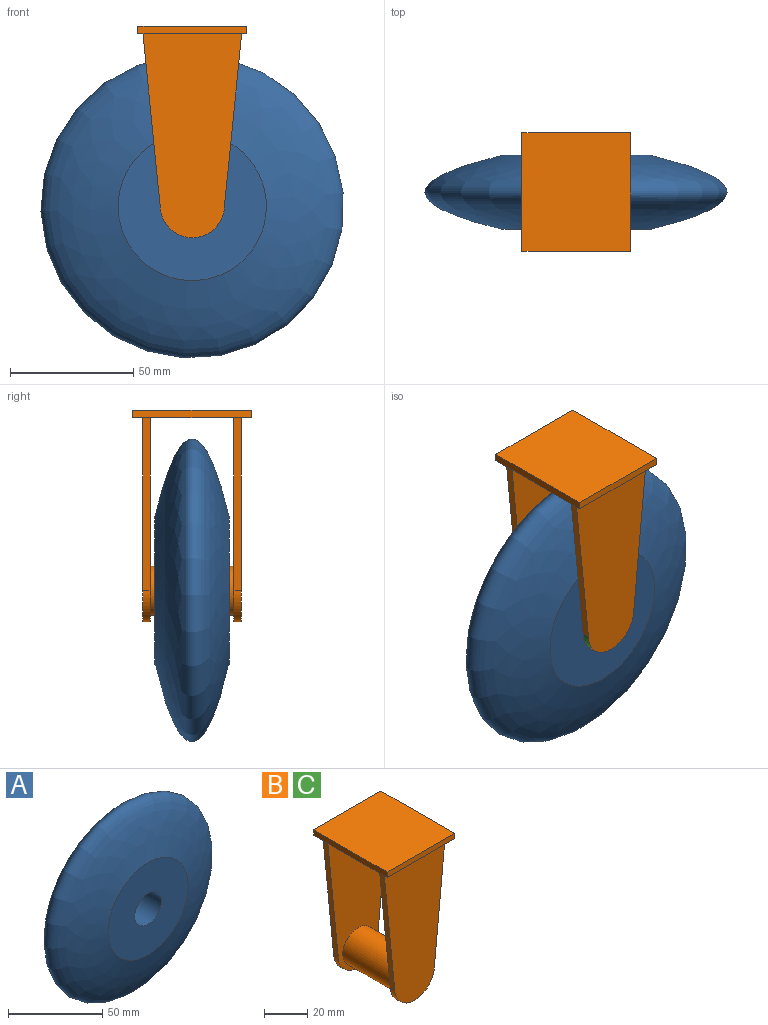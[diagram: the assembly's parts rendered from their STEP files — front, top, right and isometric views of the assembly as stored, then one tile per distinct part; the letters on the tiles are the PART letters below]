
ASSEMBLY  parts=3 mates=1
PART A: 4 faces, bbox 122.7x30x122.7 mm
  f0: plane 60x60mm, normal (0,1,0), area 2513.3mm2, adj f1,f3
  f1: cylinder r=10mm len=30mm, axis (0,1,0), area 1885mm2, adj f0,f2
  f2: plane 60x60mm, normal (0,-1,0), area 2513.3mm2, adj f1,f3
  f3: revolved ~122.66x122.66mm, area 21283.1mm2, adj f0,f2
PART B: 17 faces, bbox 44x48x85.7 mm
  f0: cylinder r=10mm len=34mm, axis (0,1,0), area 2136.3mm2, adj f4,f9
  f1: plane 70x7.01mm, normal (-1,0,-0.1), area 211.1mm2, adj f2,f4,f5,f11
  f2: cylinder r=13mm len=25.99mm, axis (0,-1,0), area 120.5mm2, adj f1,f3,f4,f5
  f3: plane 70x7mm, normal (1,0,-0.1), area 211mm2, adj f2,f4,f5,f11
  f4: plane 82.66x40mm, normal (0,1,0), area 2252.1mm2, adj f0,f1,f2,f3,f11
  f5: plane 82.66x40mm, normal (0,-1,0), area 2566.2mm2, adj f1,f2,f3,f11
  f6: plane 70x7.01mm, normal (-1,0,-0.1), area 211.1mm2, adj f7,f9,f10,f11
  f7: cylinder r=13mm len=25.99mm, axis (0,1,0), area 120.5mm2, adj f6,f8,f9,f10
  f8: plane 70x7mm, normal (1,0,-0.1), area 211mm2, adj f7,f9,f10,f11
  f9: plane 82.66x40mm, normal (0,-1,0), area 2252.1mm2, adj f0,f6,f7,f8,f11
  f10: plane 82.66x40mm, normal (0,1,0), area 2566.2mm2, adj f6,f7,f8,f11
  f11: plane 48x44mm, normal (0,0,-1), area 1872mm2, adj f1,f3,f4,f5,f6,f8,f9,f10
  f12: plane 44x3mm, normal (0,1,0), area 132mm2, adj f11,f13,f15,f16
  f13: plane 48x3mm, normal (-1,0,0), area 144mm2, adj f11,f12,f14,f16
  f14: plane 44x3mm, normal (0,-1,0), area 132mm2, adj f11,f13,f15,f16
  f15: plane 48x3mm, normal (1,0,0), area 144mm2, adj f11,f12,f14,f16
  f16: plane 48x44mm, normal (0,0,1), area 2112mm2, adj f12,f13,f14,f15
PART C: same geometry as B
PLACE A t=(-39.25,44.98,71.29)mm
PLACE B t=(-39.25,44.98,71.29)mm
PLACE C t=(-39.25,44.98,71.29)mm
MATE slider A.f1 <-> C.f0  axis (0,1,0) through (-39.25,44.98,71.29)mm
